# Revit family: FU_Inspec_Area_8-2
name_source: partatom
category: Furniture
units: mm (PartAtom-declared; Revit-internal decimal feet)

## family parameters
Always vertical = Yes
Cut with Voids When Loaded = No
OmniClass Number = 23.40.20.00
OmniClass Title = General Furniture and Specialties
Room Calculation Point = No
Shared = No
Work Plane-Based = No

## types (1)
- Colour - Black
    Assembly Code = E2020
    Default Elevation = 0 mm  [stored 0 ft]
    Description = Table of powder coated solid steel with 2 mm powder coated perforated steel sheet and powder coated tubular steel base
    Keynote = 46.B
    Legs Material = Metal - Back - Matte
    Manufacturer = Inspec
    Model = area 8.2
    Table Edge Material = Metal - Back - Matte - Net
    Table Top Material = Metal - Back - Matte - Net
    URL = https://inspecfurniture.com

note: [stored X ft] marks values corroborated as IEEE doubles in the binary element streams (Revit-internal decimal feet)

## geometry (parser evidence)
native form markers: Sweep x3
no freeform markers — native parametric forms only
